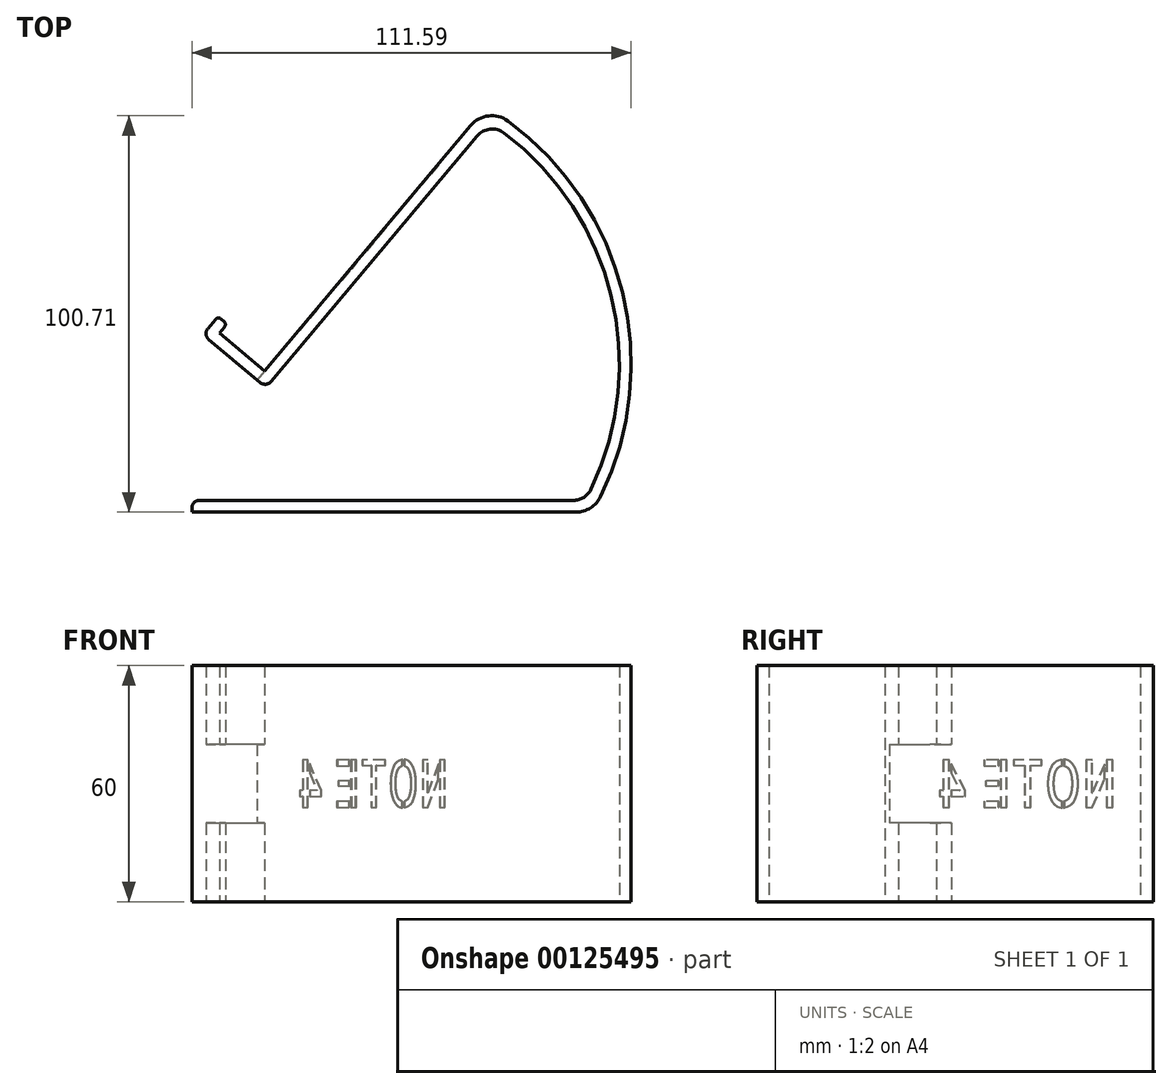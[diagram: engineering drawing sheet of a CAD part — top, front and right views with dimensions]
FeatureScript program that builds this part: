
annotation { "Feature Type Name" : "Feature", "Feature Type Description" : "" }
export const myFeature = defineFeature(function(context is Context, id is Id, definition is map)
    precondition{}
    {
        {
            var Q0;
            Q0=qCreatedBy(makeId("Top.planeOp"),FACE);
            var sketch = newSketch(context, id + "F0", { "sketchPlane" : qUnion([Q0])});
            skLineSegment(sketch, "E0", {"start": v(-82.16, -55.13) * mm, "end": v(12.76, -55.13) * mm});
            skArc(sketch, "E1", {"start": v(17.28, -52.28) * mm, "mid": v(22.32, -3.1) * mm, "end": v(-4.85, 38.2) * mm});
            skLineSegment(sketch, "E2", {"start": v(-11.7, 37.43) * mm, "end": v(-64.03, -24.95) * mm});
            skLineSegment(sketch, "E3", {"start": v(-66.85, -25.2) * mm, "end": v(-79.87, -14.27) * mm});
            skLineSegment(sketch, "E4", {"start": v(-84.16, -57.13) * mm, "end": v(-84.16, -58.13) * mm});
            skLineSegment(sketch, "E5", {"start": v(-84.16, -58.13) * mm, "end": v(13.4, -58.13) * mm});
            skArc(sketch, "E6", {"start": v(19.68, -54.2) * mm, "mid": v(25.19, -2.22) * mm, "end": v(-3.88, 41.22) * mm});
            skLineSegment(sketch, "E7", {"start": v(-80.12, -11.45) * mm, "end": v(-78.19, -9.15) * mm});
            skLineSegment(sketch, "E8", {"start": v(-65.69, -22.25) * mm, "end": v(-13.38, 40.08) * mm});
            skPoint(sketch, "E9.visualSharp", {"position": v(-9.35, 44.89) * mm});
            skArc(sketch, "E9.filletArc", {"start": v(-3.88, 41.22) * mm, "mid": v(-8.86, 42.53) * mm, "end": v(-13.38, 40.08) * mm});
            skPoint(sketch, "E10.visualSharp", {"position": v(-8.74, 40.95) * mm});
            skArc(sketch, "E10.filletArc", {"start": v(-4.85, 38.2) * mm, "mid": v(-8.42, 39.18) * mm, "end": v(-11.7, 37.43) * mm});
            skPoint(sketch, "E11.visualSharp", {"position": v(-65.32, -26.48) * mm});
            skArc(sketch, "E11.filletArc", {"start": v(-66.85, -25.2) * mm, "mid": v(-65.39, -25.65) * mm, "end": v(-64.03, -24.95) * mm});
            skPoint(sketch, "E12.visualSharp", {"position": v(-81.28, -13.09) * mm});
            skArc(sketch, "E12.filletArc", {"start": v(-80.12, -11.45) * mm, "mid": v(-80.58, -12.9) * mm, "end": v(-79.87, -14.27) * mm});
            skPoint(sketch, "E13.visualSharp", {"position": v(-84.16, -55.13) * mm});
            skArc(sketch, "E13.filletArc", {"start": v(-82.16, -55.13) * mm, "mid": v(-83.57, -55.72) * mm, "end": v(-84.16, -57.13) * mm});
            skPoint(sketch, "E14.visualSharp", {"position": v(15.84, -55.13) * mm});
            skArc(sketch, "E14.filletArc", {"start": v(12.76, -55.13) * mm, "mid": v(15.43, -54.36) * mm, "end": v(17.28, -52.28) * mm});
            skPoint(sketch, "E15.visualSharp", {"position": v(17.63, -58.13) * mm});
            skArc(sketch, "E15.filletArc", {"start": v(13.4, -58.13) * mm, "mid": v(17.1, -57.07) * mm, "end": v(19.68, -54.2) * mm});
            skLineSegment(sketch, "E16", {"start": v(-65.69, -22.25) * mm, "end": v(-77.18, -12.61) * mm});
            skLineSegment(sketch, "E17", {"start": v(-77.18, -12.61) * mm, "end": v(-75.9, -11.08) * mm});
            skLineSegment(sketch, "E18", {"start": v(-76.01, -9.67) * mm, "end": v(-76.78, -9.03) * mm});
            skPoint(sketch, "E19.visualSharp", {"position": v(-75.25, -10.31) * mm});
            skArc(sketch, "E19.filletArc", {"start": v(-75.9, -11.08) * mm, "mid": v(-75.66, -10.35) * mm, "end": v(-76.01, -9.67) * mm});
            skPoint(sketch, "E20.visualSharp", {"position": v(-77.55, -8.38) * mm});
            skArc(sketch, "E20.filletArc", {"start": v(-76.78, -9.03) * mm, "mid": v(-77.51, -8.8) * mm, "end": v(-78.19, -9.15) * mm});
            skSolve(sketch);
        }
        {
            var Q0;
            Q0=makeQuery(id+"F0.imprint","IMPRINT",FACE,{"disambiguationData":[TD([[makeQuery(id+"F0.imprint","IMPRINT",EDGE,{"derivedFrom":sQuery(id+"F0.wireOp",EDGE,"E0")}),-1.0]])]});
            extrude(context, id + "F1", {"entities" : qUnion([Q0]), "depth" : 60 * mm});
        }
        {
            var Q0;
            Q0=makeQuery(id+"F1.opExtrude","SWEPT_FACE",FACE,{"disambiguationData":[OSD([sQuery(id+"F0.wireOp",EDGE,"E7")])]});
            var sketch = newSketch(context, id + "F2", { "sketchPlane" : qUnion([Q0])});
            skLineSegment(sketch, "E21.bottom", {"start": v(52.54, 20) * mm, "end": v(66.8, 20) * mm});
            skLineSegment(sketch, "E21.top", {"start": v(66.8, 40) * mm, "end": v(52.54, 40) * mm});
            skLineSegment(sketch, "E21.left", {"start": v(52.54, 20) * mm, "end": v(52.54, 40) * mm});
            skLineSegment(sketch, "E21.right", {"start": v(66.8, 20) * mm, "end": v(66.8, 40) * mm});
            skSolve(sketch);
        }
        {
            var Q0;
            {var subQ0=sQuery(id+"F2.wireOp",EDGE,"E21.bottom");var subQ1=sQuery(id+"F0.wireOp",EDGE,"E7");var subQ2=makeQuery(id+"F1.opExtrude","SWEPT_EDGE",EDGE,{"disambiguationData":[OSD([subQ1,sQuery(id+"F0.wireOp",EDGE,"E18")])]});var subQ3=makeQuery(id+"F2.imprint","INTERSECT",VERTEX,{"derivedFrom":[subQ2,subQ0]});Q0=makeQuery(id+"F2.imprint","IMPRINT",FACE,{"disambiguationData":[TD([[makeQuery(id+"F2.imprint","IMPRINT",EDGE,{"disambiguationData":[TD([[subQ3,-1.0]])],"derivedFrom":subQ0}),1.0]])]});}
            var Q1;
            {var subQ0=sQuery(id+"F2.wireOp",EDGE,"E21.right");Q1=makeQuery(id+"F2.imprint","IMPRINT",FACE,{"disambiguationData":[TD([[makeQuery(id+"F2.imprint","IMPRINT",EDGE,{"derivedFrom":subQ0}),1.0]])]});}
            var Q2;
            {var subQ0=sQuery(id+"F2.wireOp",EDGE,"E21.left");Q2=makeQuery(id+"F2.imprint","IMPRINT",FACE,{"disambiguationData":[TD([[makeQuery(id+"F2.imprint","IMPRINT",EDGE,{"derivedFrom":subQ0}),-1.0]])]});}
            extrude(context, id + "F3", {"entities" : qUnion([Q0, Q1, Q2]), "operationType" : NewBodyOperationType.REMOVE, "oppositeDirection" : true, "depth" : 18 * mm});
        }
        {
            var Q0;
            Q0=makeQuery(id+"F3.boolean.opBoolean","MERGE",FACE,{"derivedFrom":[makeQuery(id+"F1.opExtrude","SWEPT_FACE",FACE,{"disambiguationData":[OSD([sQuery(id+"F0.wireOp",EDGE,"E8")])]}),makeQuery(id+"F3.opExtrude","CAP_FACE",FACE,{"disambiguationData":[OSD([sQuery(id+"F2.wireOp",EDGE,"E21.bottom"),sQuery(id+"F2.wireOp",EDGE,"E21.top"),sQuery(id+"F2.wireOp",EDGE,"E21.left"),sQuery(id+"F2.wireOp",EDGE,"E21.right")])],"isStart":false})]});
            var sketch = newSketch(context, id + "F4", { "sketchPlane" : qUnion([Q0])});
            skText(sketch, "E22", { "text": "NOTE 4", "fontName": "AllertaStencil-Regular.ttf"});
            const initialGuessF4  = {"E22": [-0.01337, 0.02396, 1, 0, 0.01204]};
            skSetInitialGuess(sketch, initialGuessF4);
            skSolve(sketch);
        }
        {
            var Q0;
            Q0 = qSketchRegion(id + "F4", true);
            extrude(context, id + "F5", {"entities" : qUnion([Q0]), "operationType" : NewBodyOperationType.REMOVE, "oppositeDirection" : true, "depth" : 0.2 * mm});
        }
    });
